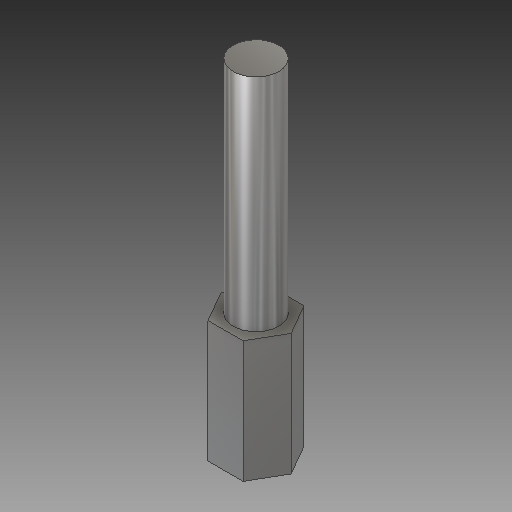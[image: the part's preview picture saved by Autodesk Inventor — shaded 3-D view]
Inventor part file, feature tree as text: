
AUTODESK INVENTOR PART (.ipt)
format: ipt  version: 2017 SP1 (Build 210196100, 196)  size: 114,176 bytes
history: native  units: in
note: dims shown in document units (in); Inventor stores cm internally (conversion verified against a paired STEP export)
features: extrude x3, sketch x3
ambient origin geometry x8: Origin, YZ Plane, XZ Plane, XY Plane, X Axis, Y Axis, Z Axis, Center Point
bodies: Solid1 (feature_tree)
feature tree (6):
  extrude  "Extrusion1"  Depth=1.0in TaperAngle=0.0deg
  extrude  "Extrusion2"  Depth=1.8125in TaperAngle=0.0deg
  extrude  "Extrusion3"  Depth=1.0in TaperAngle=0.0deg
  sketch  "Sketch1"  dims[d0=0.5in d1=1.0in d2=0.0in]
  sketch  "Sketch2"  dims[d3=0.375in d4=1.8125in d5=0.0in]
  sketch  "Sketch3"  dims[d7=0.15in d8=1.0in d9=0.0in]
